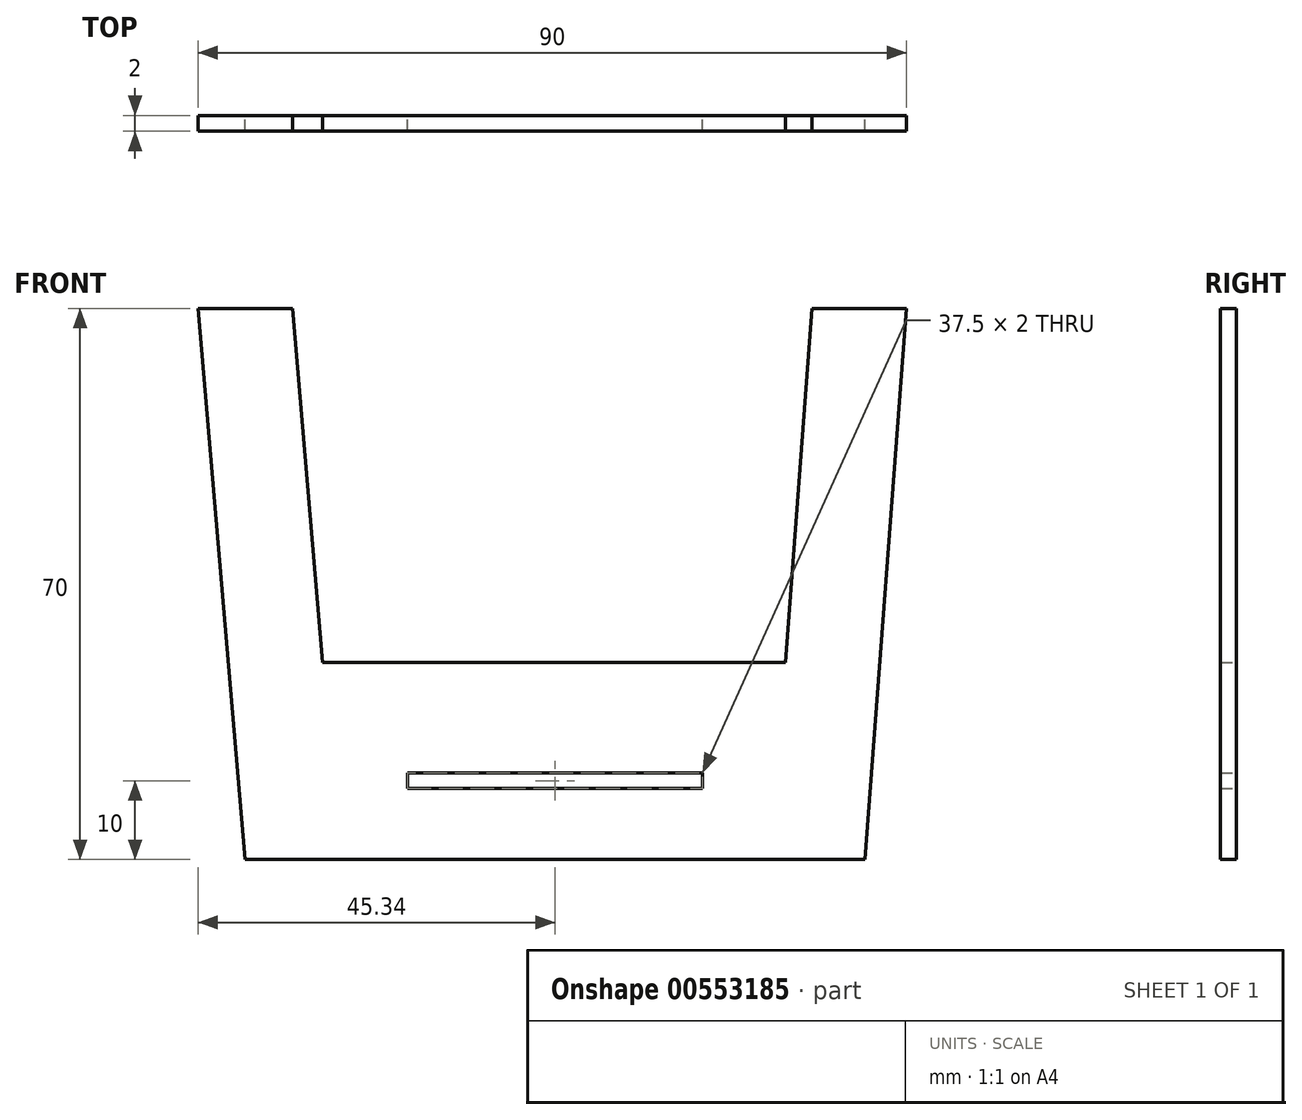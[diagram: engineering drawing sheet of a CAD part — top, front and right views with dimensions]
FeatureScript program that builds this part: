
annotation { "Feature Type Name" : "Feature", "Feature Type Description" : "" }
export const myFeature = defineFeature(function(context is Context, id is Id, definition is map)
    precondition{}
    {
        {
            var Q0;
            Q0=qCreatedBy(makeId("Front.planeOp"),FACE);
            var sketch = newSketch(context, id + "F0", { "sketchPlane" : qUnion([Q0])});
            skPoint(sketch, "E0.middle", {"position": v(0, 0) * mm});
            skLineSegment(sketch, "E1", {"start": v(0, 0) * mm, "end": v(39.38, 0) * mm});
            skLineSegment(sketch, "E2", {"start": v(0, 0) * mm, "end": v(-39.38, 0) * mm});
            skLineSegment(sketch, "E3", {"start": v(-45.34, 70) * mm, "end": v(-39.38, 0) * mm});
            skLineSegment(sketch, "E4", {"start": v(39.37, 0) * mm, "end": v(44.66, 70) * mm});
            skLineSegment(sketch, "E5", {"start": v(-45.34, 70) * mm, "end": v(-33.34, 70) * mm});
            skLineSegment(sketch, "E6", {"start": v(44.66, 70) * mm, "end": v(32.66, 70) * mm});
            skLineSegment(sketch, "E7", {"start": v(-33.34, 70) * mm, "end": v(-29.5, 25) * mm});
            skLineSegment(sketch, "E8", {"start": v(32.66, 70) * mm, "end": v(29.26, 25) * mm});
            skLineSegment(sketch, "E9", {"start": v(-29.5, 25) * mm, "end": v(29.26, 25) * mm});
            skLineSegment(sketch, "E10.bottom", {"start": v(18.75, 11) * mm, "end": v(-18.75, 11) * mm});
            skLineSegment(sketch, "E10.top", {"start": v(18.75, 9) * mm, "end": v(-18.75, 9) * mm});
            skLineSegment(sketch, "E10.left", {"start": v(18.75, 11) * mm, "end": v(18.75, 9) * mm});
            skLineSegment(sketch, "E10.right", {"start": v(-18.75, 11) * mm, "end": v(-18.75, 9) * mm});
            skPoint(sketch, "E10.middle", {"position": v(0, 10) * mm});
            skLineSegment(sketch, "E11", {"start": v(0, 0) * mm, "end": v(0, 10) * mm});
            skSolve(sketch);
        }
        {
            var Q0;
            Q0=makeQuery(id+"F0.imprint","IMPRINT",FACE,{"disambiguationData":[TD([[makeQuery(id+"F0.imprint","IMPRINT",EDGE,{"derivedFrom":sQuery(id+"F0.wireOp",EDGE,"E1")}),1.0]])]});
            extrude(context, id + "F1", {"entities" : qUnion([Q0]), "depth" : 2 * mm, "offsetDistance" : 25 * mm});
        }
    });
